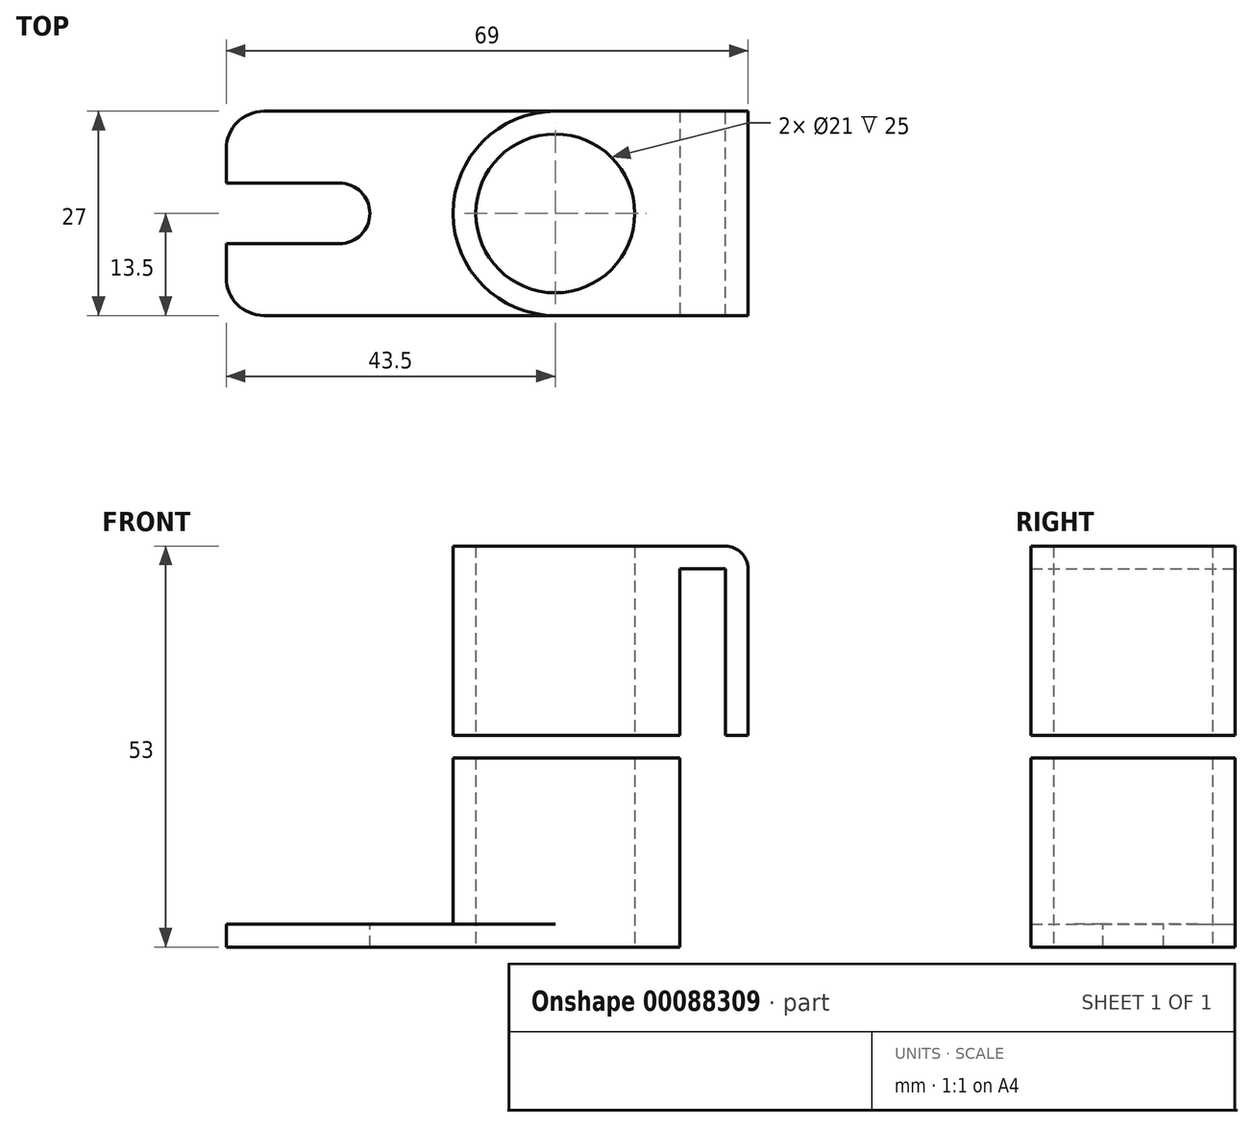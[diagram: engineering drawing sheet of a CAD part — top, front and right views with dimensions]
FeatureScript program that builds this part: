
annotation { "Feature Type Name" : "Feature", "Feature Type Description" : "" }
export const myFeature = defineFeature(function(context is Context, id is Id, definition is map)
    precondition{}
    {
        {
            var Q0;
            Q0=qCreatedBy(makeId("Top.planeOp"),FACE);
            var sketch = newSketch(context, id + "F0", { "sketchPlane" : qUnion([Q0])});
            skCircle(sketch, "E0", {"center": v(0, 0) * mm, "radius": 10.5 * mm});
            skCircle(sketch, "E1", {"center": v(0, 0) * mm, "radius": 13.5 * mm});
            skLineSegment(sketch, "E2", {"start": v(0, 13.5) * mm, "end": v(25.5, 13.5) * mm});
            skLineSegment(sketch, "E3", {"start": v(25.5, 13.5) * mm, "end": v(25.5, -13.5) * mm});
            skLineSegment(sketch, "E4", {"start": v(0, -13.5) * mm, "end": v(25.5, -13.5) * mm});
            skLineSegment(sketch, "E5", {"start": v(13.5, 0) * mm, "end": v(13.5, 13.5) * mm});
            skLineSegment(sketch, "E6", {"start": v(13.5, 0) * mm, "end": v(13.5, -13.5) * mm});
            skLineSegment(sketch, "E7", {"start": v(16.5, 13.5) * mm, "end": v(16.5, -13.5) * mm, "construction": true});
            skLineSegment(sketch, "E8", {"start": v(22.5, 13.5) * mm, "end": v(22.5, -13.5) * mm, "construction": true});
            skLineSegment(sketch, "E9", {"start": v(16.5, 13.5) * mm, "end": v(16.5, -13.5) * mm});
            skLineSegment(sketch, "E10", {"start": v(22.5, -13.5) * mm, "end": v(22.5, 13.5) * mm});
            skSolve(sketch);
        }
        {
            var Q0;
            Q0 = qSketchRegion(id + "F0", true);
            extrude(context, id + "F1", {"entities" : qUnion([Q0]), "depth" : 3 * mm});
        }
        {
            var Q0;
            Q0=makeQuery(id+"F0.imprint","IMPRINT",FACE,{"disambiguationData":[TD([[makeQuery(id+"F0.imprint","IMPRINT",EDGE,{"derivedFrom":sQuery(id+"F0.wireOp",EDGE,"E0")}),-1.0]])]});
            var Q1;
            {var subQ3=sQuery(id+"F0.wireOp",EDGE,"E5");Q1=makeQuery(id+"F0.imprint","IMPRINT",FACE,{"disambiguationData":[TD([[makeQuery(id+"F0.imprint","IMPRINT",EDGE,{"derivedFrom":subQ3}),1.0]])]});}
            var Q2;
            {var subQ1=sQuery(id+"F0.wireOp",EDGE,"E5");Q2=makeQuery(id+"F0.imprint","IMPRINT",FACE,{"disambiguationData":[TD([[makeQuery(id+"F0.imprint","IMPRINT",EDGE,{"derivedFrom":subQ1}),-1.0]])]});}
            var Q3;
            {var subQ0=sQuery(id+"F0.wireOp",EDGE,"E3");Q3=makeQuery(id+"F0.imprint","IMPRINT",FACE,{"disambiguationData":[TD([[makeQuery(id+"F0.imprint","IMPRINT",EDGE,{"derivedFrom":subQ0}),-1.0]])]});}
            var Q4;
            {var subQ3=sQuery(id+"F0.wireOp",EDGE,"E6");Q4=makeQuery(id+"F0.imprint","IMPRINT",FACE,{"disambiguationData":[TD([[makeQuery(id+"F0.imprint","IMPRINT",EDGE,{"derivedFrom":subQ3}),-1.0]])]});}
            extrude(context, id + "F2", {"entities" : qUnion([Q0, Q1, Q2, Q3, Q4]), "operationType" : NewBodyOperationType.ADD, "oppositeDirection" : true, "depth" : 22 * mm});
        }
        {
            var Q0;
            Q0=makeQuery(id+"F2.opExtrude","CAP_EDGE",EDGE,{"disambiguationData":[OSD([sQuery(id+"F0.wireOp",EDGE,"E9")])],"isStart":true});
            var Q1;
            Q1=makeQuery(id+"F2.opExtrude","CAP_EDGE",EDGE,{"disambiguationData":[OSD([sQuery(id+"F0.wireOp",EDGE,"E10")])],"isStart":true});
            var Q2;
            Q2=makeQuery(id+"F1.opExtrude","CAP_EDGE",EDGE,{"disambiguationData":[OSD([sQuery(id+"F0.wireOp",EDGE,"E3")])],"isStart":false});
            fillet(context, id + "F3", {"entities" : qUnion([Q0, Q1, Q2]), "radius" : 3 * mm, "tangentPropagation" : true, "allowEdgeOverflow" : false});
        }
        {
            var Q0;
            Q0=makeQuery(id+"F2.opExtrude","CAP_FACE",FACE,{"disambiguationData":[OSD([sQuery(id+"F0.wireOp",EDGE,"E0"),sQuery(id+"F0.wireOp",EDGE,"E1"),sQuery(id+"F0.wireOp",EDGE,"E2"),sQuery(id+"F0.wireOp",EDGE,"E4"),sQuery(id+"F0.wireOp",EDGE,"E9")])],"isStart":false});
            cPlane(context, id + "F4", {"entities" : qUnion([Q0]), "cplaneType" : CPlaneType.OFFSET, "offset" : 25 * mm, "width" : 150 * mm, "height" : 150 * mm});
        }
        {
            var Q0;
            Q0=qCreatedBy(id+"F4.planeOp",FACE);
            var sketch = newSketch(context, id + "F5", { "sketchPlane" : qUnion([Q0])});
            skCircle(sketch, "E11.0", {"center": v(0, 0) * mm, "radius": 10.5 * mm});
            skArc(sketch, "E12.0.0", {"start": v(0, 13.5) * mm, "mid": v(-13.5, 0) * mm, "end": v(0, -13.5) * mm});
            skLineSegment(sketch, "E12.0.1", {"start": v(0, -13.5) * mm, "end": v(16.5, -13.5) * mm});
            skLineSegment(sketch, "E12.0.2", {"start": v(16.5, -13.5) * mm, "end": v(16.5, 13.5) * mm});
            skLineSegment(sketch, "E12.0.3", {"start": v(16.5, 13.5) * mm, "end": v(0, 13.5) * mm});
            skLineSegment(sketch, "E13", {"start": v(0, -13.5) * mm, "end": v(-43.5, -13.5) * mm});
            skLineSegment(sketch, "E14", {"start": v(-43.5, -13.5) * mm, "end": v(-43.5, -4) * mm});
            skLineSegment(sketch, "E15", {"start": v(-43.5, 13.5) * mm, "end": v(0, 13.5) * mm});
            skLineSegment(sketch, "E16.bottom", {"start": v(0, 0) * mm, "end": v(-28.5, 0) * mm, "construction": true});
            skLineSegment(sketch, "E16.top", {"start": v(0, 4) * mm, "end": v(-43.5, 4) * mm, "construction": true});
            skLineSegment(sketch, "E16.left", {"start": v(0, 0) * mm, "end": v(0, 4) * mm, "construction": true});
            skLineSegment(sketch, "E17.MirrorCS", {"start": v(0, -4) * mm, "end": v(-43.5, -4) * mm, "construction": true});
            skLineSegment(sketch, "E18", {"start": v(-43.5, 0) * mm, "end": v(-13.5, 0) * mm, "construction": true});
            skPoint(sketch, "E19", {"position": v(-28.5, 0) * mm});
            skArc(sketch, "E20", {"start": v(-28.5, -4) * mm, "mid": v(-24.5, 0) * mm, "end": v(-28.5, 4) * mm});
            skLineSegment(sketch, "E21", {"start": v(-28.5, 4) * mm, "end": v(-43.5, 4) * mm});
            skLineSegment(sketch, "E22", {"start": v(-43.5, -4) * mm, "end": v(-28.5, -4) * mm});
            skLineSegment(sketch, "E23.trimOffspring", {"start": v(-43.5, 4) * mm, "end": v(-43.5, 13.5) * mm});
            skSolve(sketch);
        }
        {
            var Q0;
            Q0=makeQuery(id+"F5.imprint","IMPRINT",FACE,{"disambiguationData":[TD([[makeQuery(id+"F5.imprint","IMPRINT",EDGE,{"derivedFrom":sQuery(id+"F5.wireOp",EDGE,"E11.0")}),-1.0]])]});
            extrude(context, id + "F6", {"entities" : qUnion([Q0]), "oppositeDirection" : true, "depth" : 22 * mm});
        }
        {
            var Q0;
            Q0 = qSketchRegion(id + "F5", true);
            extrude(context, id + "F7", {"entities" : qUnion([Q0]), "operationType" : NewBodyOperationType.ADD, "depth" : 3 * mm});
        }
        {
            var Q0;
            Q0=makeQuery(id+"F7.opExtrude","SWEPT_EDGE",EDGE,{"disambiguationData":[OSD([sQuery(id+"F5.wireOp",EDGE,"E15"),sQuery(id+"F5.wireOp",EDGE,"E23.trimOffspring")])]});
            var Q1;
            Q1=makeQuery(id+"F7.opExtrude","SWEPT_EDGE",EDGE,{"disambiguationData":[OSD([sQuery(id+"F5.wireOp",EDGE,"E13"),sQuery(id+"F5.wireOp",EDGE,"E14")])]});
            fillet(context, id + "F8", {"entities" : qUnion([Q0, Q1]), "radius" : 5 * mm, "tangentPropagation" : true, "allowEdgeOverflow" : false});
        }
    });
